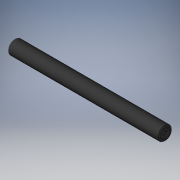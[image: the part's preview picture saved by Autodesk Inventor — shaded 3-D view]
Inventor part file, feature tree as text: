
AUTODESK INVENTOR PART (.ipt)
format: ipt  version: 2019 (Build 230136000, 136)  size: 122,880 bytes
history: native  units: mm
features: sketch x3, hole x2, revolve x1
ambient origin geometry x8: Origin, YZ Plane, XZ Plane, XY Plane, X Axis, Y Axis, Z Axis, Center Point
bodies: Solid1 (feature_tree)
feature tree (6):
  revolve  "Revolution1"  [1 undecoded]
  hole  "Hole1"  [1 undecoded]
  hole  "Hole2"  [1 undecoded]
  sketch  "Sketch_1"  dims[d0=360.0deg]
  sketch  "Sketch2"  dims[d1=3.242mm d2=8.0mm d3=4.0mm d4=2.0mm d5=90.0deg d6=9.064115mm d7=120.0deg]
  sketch  "Sketch3"  dims[d8=3.242mm d9=8.0mm d10=4.0mm d11=2.0mm d12=90.0deg d13=9.024115mm d14=120.0deg]
note: 3 required parameter values undecoded (feature->parameter linkage not recoverable at this tier; creation-order binding heuristic only, values carry confidence <= 0.55)
